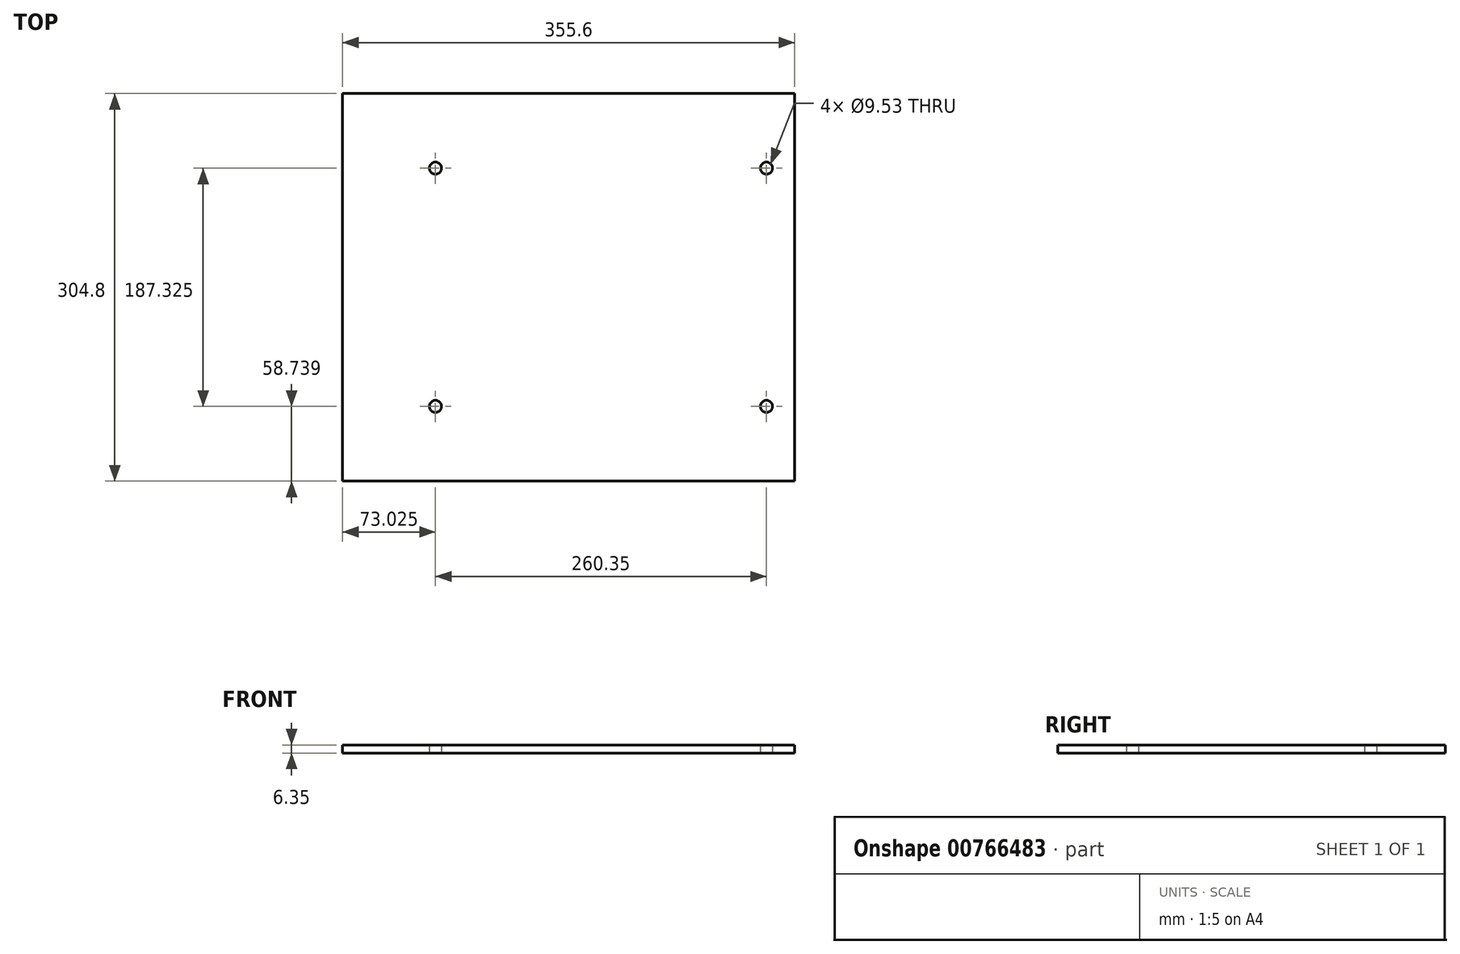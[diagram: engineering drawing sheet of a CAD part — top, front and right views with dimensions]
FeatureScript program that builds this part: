
annotation { "Feature Type Name" : "Feature", "Feature Type Description" : "" }
export const myFeature = defineFeature(function(context is Context, id is Id, definition is map)
    precondition{}
    {
        {
            var Q0;
            Q0=qCreatedBy(makeId("Top.planeOp"),FACE);
            var sketch = newSketch(context, id + "F0", { "sketchPlane" : qUnion([Q0])});
            skLineSegment(sketch, "E0.bottom", {"start": v(0, 4.6) * mm, "end": v(355.6, 4.6) * mm});
            skLineSegment(sketch, "E0.top", {"start": v(0, 309.4) * mm, "end": v(355.6, 309.4) * mm});
            skLineSegment(sketch, "E0.left", {"start": v(0, 4.6) * mm, "end": v(0, 309.4) * mm});
            skLineSegment(sketch, "E0.right", {"start": v(355.6, 4.6) * mm, "end": v(355.6, 309.4) * mm});
            skCircle(sketch, "E1", {"center": v(333.38, 63.33) * mm, "radius": 4.76 * mm});
            skCircle(sketch, "E2.0.1.0", {"center": v(333.38, 250.65) * mm, "radius": 4.76 * mm});
            skCircle(sketch, "E2.1.0.0", {"center": v(73.03, 63.33) * mm, "radius": 4.76 * mm});
            skCircle(sketch, "E2.1.1.0", {"center": v(73.03, 250.65) * mm, "radius": 4.76 * mm});
            skLineSegment(sketch, "E2.direction1", {"start": v(333.38, 63.33) * mm, "end": v(73.03, 63.33) * mm, "construction": true});
            skLineSegment(sketch, "E2.direction2", {"start": v(333.38, 63.33) * mm, "end": v(333.38, 250.65) * mm, "construction": true});
            skSolve(sketch);
        }
        {
            var Q0;
            Q0=qSketchRegion(id+"F0",true);
            extrude(context, id + "F1", {"entities" : qUnion([Q0]), "depth" : 6.35 * mm, "offsetDistance" : 25.4 * mm});
        }
    });
